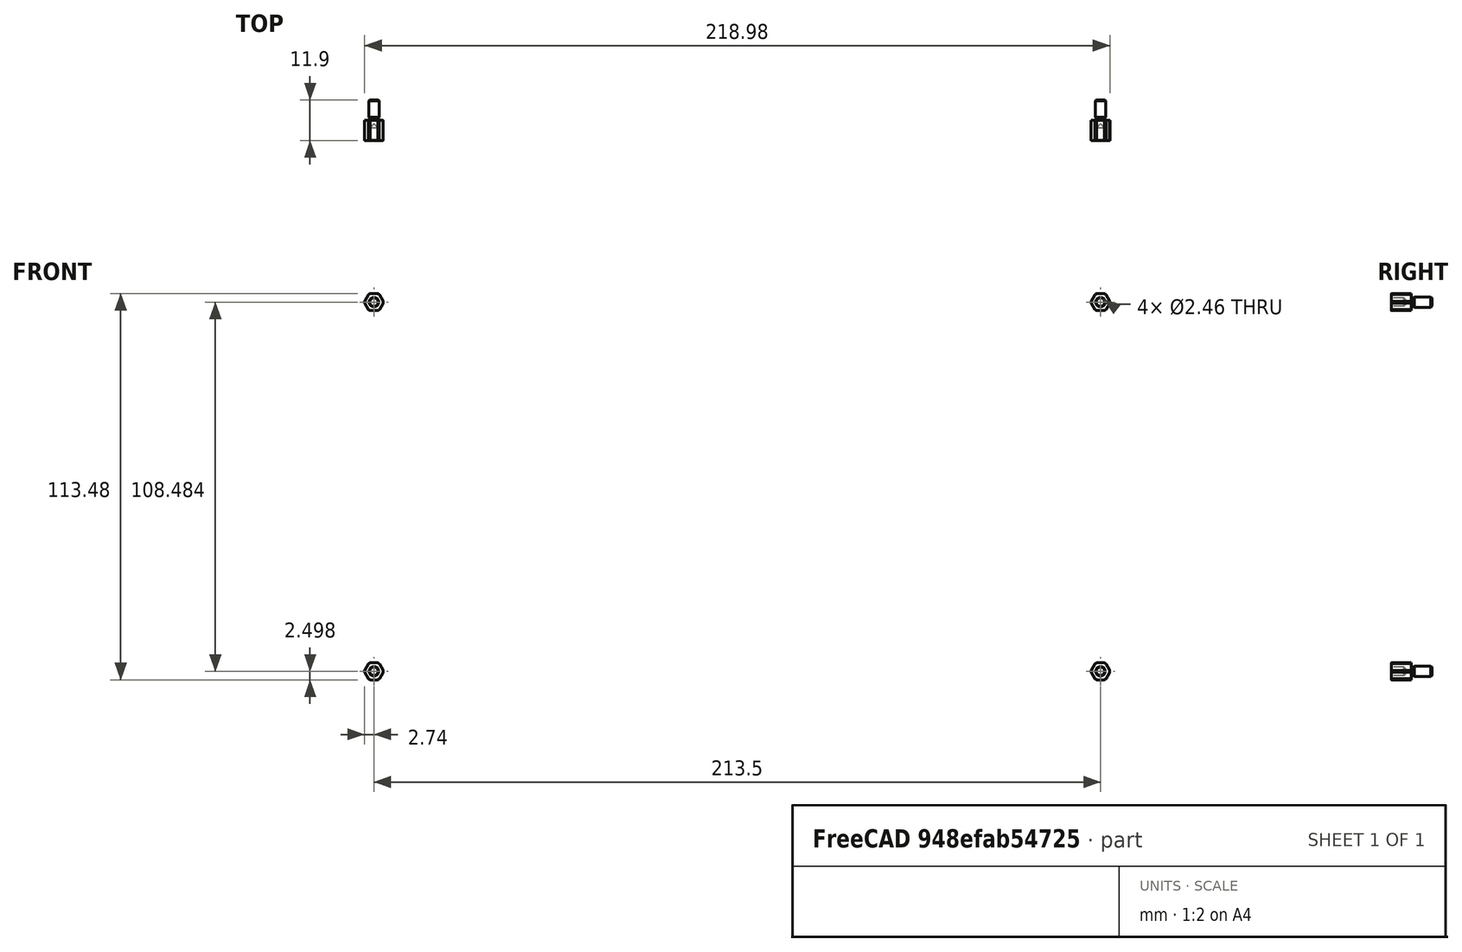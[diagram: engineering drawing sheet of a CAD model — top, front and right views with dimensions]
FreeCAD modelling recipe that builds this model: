
FCSTD DOCUMENT  (FreeCAD 1.0R38641 +468 (Git))
Label: enclosure
License: All rights reserved
LicenseURL: https://en.wikipedia.org/wiki/All_rights_reserved
objects: App::Link×58, App::FeaturePython×4, Assembly::AssemblyLink×4, Part::FeaturePython×4, Assembly::JointGroup×1, Assembly::AssemblyObject×1
note: 4 computed .brp shape members not serialized (recipe doc carries the construction recipe); baked Part::Feature solids carry a one-line shape summary decoded from their .brp
EXTERNAL_REF file=row.FCStd obj=Assembly
EXTERNAL_REF file=row.FCStd obj=ZRail84Hp
EXTERNAL_REF file=row.FCStd obj=ZRail84Hp001
EXTERNAL_REF file=row.FCStd obj=PanelSide
EXTERNAL_REF file=row.FCStd obj=PanelSide001
EXTERNAL_REF file=row.FCStd obj=PanelTopAndBottom
EXTERNAL_REF file=row.FCStd obj=PanelTopAndBottom001
EXTERNAL_REF file=row.FCStd obj=PanelBack
EXTERNAL_REF file=row.FCStd obj=FramePanelSpacer
EXTERNAL_REF file=row.FCStd obj=FramePanelSpacer001
EXTERNAL_REF file=row.FCStd obj=FrameBracket
EXTERNAL_REF file=row.FCStd obj=FrameBracket001
EXTERNAL_REF file=row.FCStd obj=FrameBracket002
EXTERNAL_REF file=row.FCStd obj=FrameBracket003
EXTERNAL_REF file=parts/dimensions.FCStd obj=VarSet
EXTERNAL_REF file=row.FCStd obj=BusBoard
EXTERNAL_REF file=psu.FCStd obj=Assembly
EXTERNAL_REF file=psu.FCStd obj=PsuTopAndBottom
EXTERNAL_REF file=psu.FCStd obj=PsuTopAndBottom001
EXTERNAL_REF file=psu.FCStd obj=PsuSideShort
EXTERNAL_REF file=psu.FCStd obj=PsuSideShort001
EXTERNAL_REF file=psu.FCStd obj=PsuSideLong
EXTERNAL_REF file=psu.FCStd obj=PsuSideLong001
EXTERNAL_REF file=psu.FCStd obj=PowerEntry
EXTERNAL_REF file=psu.FCStd obj=Psu
EXTERNAL_REF file=psu.FCStd obj=Standoff
EXTERNAL_REF file=psu.FCStd obj=Standoff001
EXTERNAL_REF file=psu.FCStd obj=Standoff002
EXTERNAL_REF file=psu.FCStd obj=Standoff003
EXTERNAL_REF file=psu.FCStd obj=Standoff004
EXTERNAL_REF file=psu.FCStd obj=Standoff005
EXTERNAL_REF file=psu.FCStd obj=Standoff006
EXTERNAL_REF file=psu.FCStd obj=Standoff007

FEATURE [App::Link] ZRail84Hp
  LinkedObject = -> <external row.FCStd>#ZRail84Hp
FEATURE [App::Link] ZRail84Hp001
  LinkPlacement = pos=(427,3.84e-14,-112.5) rot=(0,1,0;3.14159rad)
  LinkedObject = -> <external row.FCStd>#ZRail84Hp001
  Placement = pos=(427,3.84e-14,-112.5) rot=(0,1,0;3.14159rad)
FEATURE [App::Link] PanelSide
  LinkPlacement = pos=(2.1e-15,-4.56e-14,-3e-16) rot=(0,0,1;0rad)
  LinkedObject = -> <external row.FCStd>#PanelSide
  Placement = pos=(2.1e-15,-4.56e-14,-3e-16) rot=(0,0,1;0rad)
FEATURE [App::Link] PanelSide001
  LinkPlacement = pos=(428.854,-6e-16,4e-16) rot=(0,0,1;0rad)
  LinkedObject = -> <external row.FCStd>#PanelSide001
  Placement = pos=(428.854,-6e-16,4e-16) rot=(0,0,1;0rad)
FEATURE [App::Link] PanelTopAndBottom
  LinkPlacement = pos=(5.0165e-12,3e-16,-2.004e-13) rot=(0,0,1;0rad)
  LinkedObject = -> <external row.FCStd>#PanelTopAndBottom
  Placement = pos=(5.0165e-12,3e-16,-2.004e-13) rot=(0,0,1;0rad)
FEATURE [App::Link] PanelTopAndBottom001
  LinkPlacement = pos=(5.0396e-12,-3.3e-14,-122.5) rot=(0,0,1;0rad)
  LinkedObject = -> <external row.FCStd>#PanelTopAndBottom001
  Placement = pos=(5.0396e-12,-3.3e-14,-122.5) rot=(0,0,1;0rad)
FEATURE [App::Link] PanelBack
  LinkPlacement = pos=(5.0317e-12,1.81e-14,-2.019e-13) rot=(0,0,1;0rad)
  LinkedObject = -> <external row.FCStd>#PanelBack
  Placement = pos=(5.0317e-12,1.81e-14,-2.019e-13) rot=(0,0,1;0rad)
FEATURE [App::Link] FramePanelSpacer
  LinkPlacement = pos=(2.1e-15,-3.6e-14,-3.1e-15) rot=(0,0,1;0rad)
  LinkedObject = -> <external row.FCStd>#FramePanelSpacer
  Placement = pos=(2.1e-15,-3.6e-14,-3.1e-15) rot=(0,0,1;0rad)
FEATURE [App::Link] FramePanelSpacer001
  LinkPlacement = pos=(433.883,-1.9e-15,2.7e-15) rot=(0,0,1;0rad)
  LinkedObject = -> <external row.FCStd>#FramePanelSpacer001
  Placement = pos=(433.883,-1.9e-15,2.7e-15) rot=(0,0,1;0rad)
FEATURE [App::Link] FrameBracket
  LinkPlacement = pos=(-3.175,-3.44e-14,3.4e-15) rot=(0,0,1;0rad)
  LinkedObject = -> <external row.FCStd>#FrameBracket
  Placement = pos=(-3.175,-3.44e-14,3.4e-15) rot=(0,0,1;0rad)
FEATURE [App::Link] FrameBracket001
  LinkPlacement = pos=(-13.2334,-3.72e-14,-112.5) rot=(0,1,0;3.14159rad)
  LinkedObject = -> <external row.FCStd>#FrameBracket001
  Placement = pos=(-13.2334,-3.72e-14,-112.5) rot=(0,1,0;3.14159rad)
FEATURE [App::Link] FrameBracket002
  LinkPlacement = pos=(433.35,7.3e-15,-112.5) rot=(0,1,0;3.14159rad)
  LinkedObject = -> <external row.FCStd>#FrameBracket002
  Placement = pos=(433.35,7.3e-15,-112.5) rot=(0,1,0;3.14159rad)
FEATURE [App::Link] FrameBracket003
  LinkPlacement = pos=(437.058,3.9e-15,3.4e-15) rot=(0,0,1;0rad)
  LinkedObject = -> <external row.FCStd>#FrameBracket003
  Placement = pos=(437.058,3.9e-15,3.4e-15) rot=(0,0,1;0rad)
FEATURE [App::Link] ZRail84Hp002
  LinkedObject = -> <external row.FCStd>#ZRail84Hp
FEATURE [App::Link] ZRail84Hp003
  LinkPlacement = pos=(427,3.84e-14,-112.5) rot=(0,1,0;3.14159rad)
  LinkedObject = -> <external row.FCStd>#ZRail84Hp001
  Placement = pos=(427,3.84e-14,-112.5) rot=(0,1,0;3.14159rad)
FEATURE [App::Link] PanelSide002
  LinkPlacement = pos=(2.1e-15,-4.56e-14,-3e-16) rot=(0,0,1;0rad)
  LinkedObject = -> <external row.FCStd>#PanelSide
  Placement = pos=(2.1e-15,-4.56e-14,-3e-16) rot=(0,0,1;0rad)
FEATURE [App::Link] PanelSide003
  LinkPlacement = pos=(428.854,-6e-16,4e-16) rot=(0,0,1;0rad)
  LinkedObject = -> <external row.FCStd>#PanelSide001
  Placement = pos=(428.854,-6e-16,4e-16) rot=(0,0,1;0rad)
FEATURE [App::Link] PanelTopAndBottom002
  LinkPlacement = pos=(5.0165e-12,3e-16,-2.004e-13) rot=(0,0,1;0rad)
  LinkedObject = -> <external row.FCStd>#PanelTopAndBottom
  Placement = pos=(5.0165e-12,3e-16,-2.004e-13) rot=(0,0,1;0rad)
FEATURE [App::Link] PanelTopAndBottom003
  LinkPlacement = pos=(5.0396e-12,-3.3e-14,-122.5) rot=(0,0,1;0rad)
  LinkedObject = -> <external row.FCStd>#PanelTopAndBottom001
  Placement = pos=(5.0396e-12,-3.3e-14,-122.5) rot=(0,0,1;0rad)
FEATURE [App::Link] PanelBack001
  LinkPlacement = pos=(5.0317e-12,1.81e-14,-2.019e-13) rot=(0,0,1;0rad)
  LinkedObject = -> <external row.FCStd>#PanelBack
  Placement = pos=(5.0317e-12,1.81e-14,-2.019e-13) rot=(0,0,1;0rad)
FEATURE [App::Link] FramePanelSpacer002
  LinkPlacement = pos=(2.1e-15,-3.6e-14,-3.1e-15) rot=(0,0,1;0rad)
  LinkedObject = -> <external row.FCStd>#FramePanelSpacer
  Placement = pos=(2.1e-15,-3.6e-14,-3.1e-15) rot=(0,0,1;0rad)
FEATURE [App::Link] FramePanelSpacer003
  LinkPlacement = pos=(433.883,-1.9e-15,2.7e-15) rot=(0,0,1;0rad)
  LinkedObject = -> <external row.FCStd>#FramePanelSpacer001
  Placement = pos=(433.883,-1.9e-15,2.7e-15) rot=(0,0,1;0rad)
FEATURE [App::Link] FrameBracket004
  LinkPlacement = pos=(-3.175,-3.44e-14,3.4e-15) rot=(0,0,1;0rad)
  LinkedObject = -> <external row.FCStd>#FrameBracket
  Placement = pos=(-3.175,-3.44e-14,3.4e-15) rot=(0,0,1;0rad)
FEATURE [App::Link] FrameBracket005
  LinkPlacement = pos=(-13.2334,-3.72e-14,-112.5) rot=(0,1,0;3.14159rad)
  LinkedObject = -> <external row.FCStd>#FrameBracket001
  Placement = pos=(-13.2334,-3.72e-14,-112.5) rot=(0,1,0;3.14159rad)
FEATURE [App::Link] FrameBracket006
  LinkPlacement = pos=(433.35,7.3e-15,-112.5) rot=(0,1,0;3.14159rad)
  LinkedObject = -> <external row.FCStd>#FrameBracket002
  Placement = pos=(433.35,7.3e-15,-112.5) rot=(0,1,0;3.14159rad)
FEATURE [App::Link] FrameBracket007
  LinkPlacement = pos=(437.058,3.9e-15,3.4e-15) rot=(0,0,1;0rad)
  LinkedObject = -> <external row.FCStd>#FrameBracket003
  Placement = pos=(437.058,3.9e-15,3.4e-15) rot=(0,0,1;0rad)
FEATURE [App::FeaturePython] Joint  label="Fixed"  # Assembly joint (typed FeaturePython)
  Activated = true
  AngleMax = 0
  AngleMin = 0
  Detach1 = false
  Detach2 = false
  Distance = 0
  Distance2 = 0
  EnableAngleMax = false
  EnableAngleMin = false
  EnableLengthMax = false
  EnableLengthMin = false
  JointType = 0 (Fixed)
  LengthMax = 0
  LengthMin = 0
  Placement1 = pos=(-1.8542,-10.527,11.2) rot=(0.57735,0.57735,0.57735;2.0944rad)
  Placement2 = pos=(-1.8542,-10.527,11.2) rot=(0.57735,0.57735,0.57735;2.0944rad)
  Reference1 = -> Assembly [Row.FrameBracket003.Edge92,Row.FrameBracket003.Edge92]
  Reference2 = -> Assembly [Row001.FrameBracket006.Edge92,Row001.FrameBracket006.Edge92]
FEATURE [App::Link] ZRail84Hp004
  LinkedObject = -> <external row.FCStd>#ZRail84Hp
FEATURE [App::Link] ZRail84Hp005
  LinkPlacement = pos=(427,3.84e-14,-112.5) rot=(0,1,0;3.14159rad)
  LinkedObject = -> <external row.FCStd>#ZRail84Hp001
  Placement = pos=(427,3.84e-14,-112.5) rot=(0,1,0;3.14159rad)
FEATURE [App::Link] PanelSide004
  LinkPlacement = pos=(2.1e-15,-4.56e-14,-3e-16) rot=(0,0,1;0rad)
  LinkedObject = -> <external row.FCStd>#PanelSide
  Placement = pos=(2.1e-15,-4.56e-14,-3e-16) rot=(0,0,1;0rad)
FEATURE [App::Link] PanelSide005
  LinkPlacement = pos=(428.854,-6e-16,4e-16) rot=(0,0,1;0rad)
  LinkedObject = -> <external row.FCStd>#PanelSide001
  Placement = pos=(428.854,-6e-16,4e-16) rot=(0,0,1;0rad)
FEATURE [App::Link] PanelTopAndBottom004
  LinkPlacement = pos=(5.0165e-12,3e-16,-2.004e-13) rot=(0,0,1;0rad)
  LinkedObject = -> <external row.FCStd>#PanelTopAndBottom
  Placement = pos=(5.0165e-12,3e-16,-2.004e-13) rot=(0,0,1;0rad)
FEATURE [App::Link] PanelTopAndBottom005
  LinkPlacement = pos=(5.0396e-12,-3.3e-14,-122.5) rot=(0,0,1;0rad)
  LinkedObject = -> <external row.FCStd>#PanelTopAndBottom001
  Placement = pos=(5.0396e-12,-3.3e-14,-122.5) rot=(0,0,1;0rad)
FEATURE [App::Link] PanelBack002
  LinkPlacement = pos=(5.0317e-12,1.81e-14,-2.019e-13) rot=(0,0,1;0rad)
  LinkedObject = -> <external row.FCStd>#PanelBack
  Placement = pos=(5.0317e-12,1.81e-14,-2.019e-13) rot=(0,0,1;0rad)
FEATURE [App::Link] FramePanelSpacer004
  LinkPlacement = pos=(2.1e-15,-3.6e-14,-3.1e-15) rot=(0,0,1;0rad)
  LinkedObject = -> <external row.FCStd>#FramePanelSpacer
  Placement = pos=(2.1e-15,-3.6e-14,-3.1e-15) rot=(0,0,1;0rad)
FEATURE [App::Link] FramePanelSpacer005
  LinkPlacement = pos=(433.883,-1.9e-15,2.7e-15) rot=(0,0,1;0rad)
  LinkedObject = -> <external row.FCStd>#FramePanelSpacer001
  Placement = pos=(433.883,-1.9e-15,2.7e-15) rot=(0,0,1;0rad)
FEATURE [App::Link] FrameBracket008
  LinkPlacement = pos=(-3.175,-3.44e-14,3.4e-15) rot=(0,0,1;0rad)
  LinkedObject = -> <external row.FCStd>#FrameBracket
  Placement = pos=(-3.175,-3.44e-14,3.4e-15) rot=(0,0,1;0rad)
FEATURE [App::Link] FrameBracket009
  LinkPlacement = pos=(-13.2334,-3.72e-14,-112.5) rot=(0,1,0;3.14159rad)
  LinkedObject = -> <external row.FCStd>#FrameBracket001
  Placement = pos=(-13.2334,-3.72e-14,-112.5) rot=(0,1,0;3.14159rad)
FEATURE [App::Link] FrameBracket010
  LinkPlacement = pos=(433.35,7.3e-15,-112.5) rot=(0,1,0;3.14159rad)
  LinkedObject = -> <external row.FCStd>#FrameBracket002
  Placement = pos=(433.35,7.3e-15,-112.5) rot=(0,1,0;3.14159rad)
FEATURE [App::Link] FrameBracket011
  LinkPlacement = pos=(437.058,3.9e-15,3.4e-15) rot=(0,0,1;0rad)
  LinkedObject = -> <external row.FCStd>#FrameBracket003
  Placement = pos=(437.058,3.9e-15,3.4e-15) rot=(0,0,1;0rad)
FEATURE [App::FeaturePython] Joint001  label="Fixed001"  # Assembly joint (typed FeaturePython)
  Activated = true
  AngleMax = 0
  AngleMin = 0
  Detach1 = false
  Detach2 = false
  Distance = 0
  Distance2 = 0
  EnableAngleMax = false
  EnableAngleMin = false
  EnableLengthMax = false
  EnableLengthMin = false
  JointType = 0 (Fixed)
  LengthMax = 0
  LengthMin = 0
  Offset2 = pos=(0,0,0) rot=(0,0,1;0.392699rad)
  Placement1 = pos=(-1.8542,-10.3247,9.14628) rot=(0.57735,0.57735,0.57735;2.0944rad)
  Placement2 = pos=(-1.8542,-10.3247,9.14628) rot=(0.639338,0.427192,0.639338;2.33414rad)
  Reference1 = -> Assembly [Row002.FrameBracket010.Edge87,Row002.FrameBracket010.Edge87]
  Reference2 = -> Assembly [Row001.FrameBracket007.Edge87,Row001.FrameBracket007.Edge87]
  expr: .Offset2.Rotation.Yaw = dimensions#VarSet.MaxAngle
FEATURE [App::Link] BusBoard
  LinkPlacement = pos=(17.92,121.373,-77.205) rot=(1,0,0;1.5708rad)
  LinkedObject = -> <external row.FCStd>#BusBoard
  Placement = pos=(17.92,121.373,-77.205) rot=(1,0,0;1.5708rad)
FEATURE [Assembly::AssemblyLink] Row
  Group = -> [ZRail84Hp,ZRail84Hp001,PanelSide,PanelSide001,PanelTopAndBottom,PanelTopAndBottom001,PanelBack,FramePanelSpacer,FramePanelSpacer001,FrameBracket,FrameBracket001,FrameBracket002,FrameBracket003,BusBoard]
  LinkedObject = -> <external row.FCStd>#Assembly
  Origin = -> Origin001
  Rigid = true
FEATURE [App::FeaturePython] GroundedJoint  # Assembly grounded joint (typed FeaturePython)
  ObjectToGround = -> Row
FEATURE [App::Link] BusBoard001
  LinkPlacement = pos=(17.92,121.373,-77.205) rot=(1,0,0;1.5708rad)
  LinkedObject = -> <external row.FCStd>#BusBoard
  Placement = pos=(17.92,121.373,-77.205) rot=(1,0,0;1.5708rad)
FEATURE [Assembly::AssemblyLink] Row001
  Group = -> [ZRail84Hp002,ZRail84Hp003,PanelSide002,PanelSide003,PanelTopAndBottom002,PanelTopAndBottom003,PanelBack001,FramePanelSpacer002,FramePanelSpacer003,FrameBracket004,FrameBracket005,FrameBracket006,FrameBracket007,BusBoard001]
  LinkedObject = -> <external row.FCStd>#Assembly
  Origin = -> Origin002
  Placement = pos=(2.03e-14,4.768e-13,134.9) rot=(0,0,1;0rad)
  Rigid = true
FEATURE [App::Link] BusBoard002
  LinkPlacement = pos=(17.92,121.373,-77.205) rot=(1,0,0;1.5708rad)
  LinkedObject = -> <external row.FCStd>#BusBoard
  Placement = pos=(17.92,121.373,-77.205) rot=(1,0,0;1.5708rad)
FEATURE [Assembly::AssemblyLink] Row002
  Group = -> [ZRail84Hp004,ZRail84Hp005,PanelSide004,PanelSide005,PanelTopAndBottom004,PanelTopAndBottom005,PanelBack002,FramePanelSpacer004,FramePanelSpacer005,FrameBracket008,FrameBracket009,FrameBracket010,FrameBracket011,BusBoard002]
  LinkedObject = -> <external row.FCStd>#Assembly
  Origin = -> Origin003
  Placement = pos=(-2.818e-13,-47.3379,260.384) rot=(1,0,0;0.392699rad)
  Rigid = true
FEATURE [Part::FeaturePython] Standoff  label="M3x6x5-Standoff"  # WARN: FeaturePython — macro-defined, semantics opaque (R4)
  BaseObject = -> Row001 [PanelBack001.Pad.Edge218]
  Diameter = 2
  Invert = false
  LeftHanded = false
  Length = 4
  LengthCustom = 6
  MatchOuter = false
  Offset = -6
  OffsetAngle = 0
  Placement = pos=(320.25,133.227,132.892) rot=(1,0,0;1.5708rad)
  ScrewLength = 6
  Thread = false
  Type = 0
  Width = 0
FEATURE [Part::FeaturePython] Standoff001  label="M3x6x5-Standoff028"  # WARN: FeaturePython — macro-defined, semantics opaque (R4)
  BaseObject = -> Row001 [PanelBack001.Pad.Edge245]
  Diameter = 2
  Invert = false
  LeftHanded = false
  Length = 4
  LengthCustom = 6
  MatchOuter = false
  Offset = -6
  OffsetAngle = 0
  Placement = pos=(106.75,133.227,132.892) rot=(1,0,0;1.5708rad)
  ScrewLength = 6
  Thread = false
  Type = 0
  Width = 0
FEATURE [Part::FeaturePython] Standoff002  label="M3x6x5-Standoff029"  # WARN: FeaturePython — macro-defined, semantics opaque (R4)
  BaseObject = -> Row001 [PanelBack001.Pad.Edge221]
  Diameter = 2
  Invert = false
  LeftHanded = false
  Length = 4
  LengthCustom = 6
  MatchOuter = false
  Offset = -6
  OffsetAngle = 0
  Placement = pos=(320.25,133.227,24.4081) rot=(1,0,0;1.5708rad)
  ScrewLength = 6
  Thread = false
  Type = 0
  Width = 0
FEATURE [Part::FeaturePython] Standoff003  label="M3x6x5-Standoff030"  # WARN: FeaturePython — macro-defined, semantics opaque (R4)
  BaseObject = -> Row001 [PanelBack001.Pad.Edge248]
  Diameter = 2
  Invert = false
  LeftHanded = false
  Length = 4
  LengthCustom = 6
  MatchOuter = false
  Offset = -6
  OffsetAngle = 0
  Placement = pos=(106.75,133.227,24.4081) rot=(1,0,0;1.5708rad)
  ScrewLength = 6
  Thread = false
  Type = 0
  Width = 0
FEATURE [App::Link] PsuTopAndBottom
  LinkedObject = -> <external psu.FCStd>#PsuTopAndBottom
FEATURE [App::Link] PsuTopAndBottom001
  LinkPlacement = pos=(-6e-15,-51.8542,-3e-16) rot=(0,0,1;0rad)
  LinkedObject = -> <external psu.FCStd>#PsuTopAndBottom001
  Placement = pos=(-6e-15,-51.8542,-3e-16) rot=(0,0,1;0rad)
FEATURE [App::Link] PsuSideShort
  LinkPlacement = pos=(0.127,-51.8542,1.5e-14) rot=(0,0,1;0rad)
  LinkedObject = -> <external psu.FCStd>#PsuSideShort
  Placement = pos=(0.127,-51.8542,1.5e-14) rot=(0,0,1;0rad)
FEATURE [App::Link] PsuSideShort001
  LinkPlacement = pos=(-227.198,-51.8542,1.832e-13) rot=(0,0,1;0rad)
  LinkedObject = -> <external psu.FCStd>#PsuSideShort001
  Placement = pos=(-227.198,-51.8542,1.832e-13) rot=(0,0,1;0rad)
FEATURE [App::Link] PsuSideLong
  LinkPlacement = pos=(2.22e-14,-51.8542,0.127) rot=(0,0,1;0rad)
  LinkedObject = -> <external psu.FCStd>#PsuSideLong
  Placement = pos=(2.22e-14,-51.8542,0.127) rot=(0,0,1;0rad)
FEATURE [App::Link] PsuSideLong001
  LinkPlacement = pos=(2.26e-14,-51.8542,-86.1976) rot=(0,0,1;0rad)
  LinkedObject = -> <external psu.FCStd>#PsuSideLong001
  Placement = pos=(2.26e-14,-51.8542,-86.1976) rot=(0,0,1;0rad)
FEATURE [App::Link] PowerEntry
  LinkPlacement = pos=(333.089,127.227,-56.25) rot=(0,0.707107,-0.707107;3.14159rad)
  LinkedObject = -> <external psu.FCStd>#PowerEntry
  Placement = pos=(333.089,127.227,-56.25) rot=(0,0.707107,-0.707107;3.14159rad)
FEATURE [App::Link] Psu
  LinkPlacement = pos=(103,83.2271,-16.25) rot=(-1,0,0;1.5708rad)
  LinkedObject = -> <external psu.FCStd>#Psu
  Placement = pos=(103,83.2271,-16.25) rot=(-1,0,0;1.5708rad)
FEATURE [App::Link] Standoff004  label="M3x6x5-Standoff013"
  LinkPlacement = pos=(274.5,83.2271,-21.35) rot=(1,0,0;1.5708rad)
  LinkedObject = -> <external psu.FCStd>#Standoff
  Placement = pos=(274.5,83.2271,-21.35) rot=(1,0,0;1.5708rad)
FEATURE [App::Link] Standoff005  label="M3x6x5-Standoff016"
  LinkPlacement = pos=(122.1,83.2271,-36.55) rot=(1,0,0;1.5708rad)
  LinkedObject = -> <external psu.FCStd>#Standoff001
  Placement = pos=(122.1,83.2271,-36.55) rot=(1,0,0;1.5708rad)
FEATURE [App::Link] Standoff006  label="M3x6x5-Standoff017"
  LinkPlacement = pos=(122.1,83.2271,-75.95) rot=(1,0,0;1.5708rad)
  LinkedObject = -> <external psu.FCStd>#Standoff002
  Placement = pos=(122.1,83.2271,-75.95) rot=(1,0,0;1.5708rad)
FEATURE [App::Link] Standoff007  label="M3x6x5-Standoff018"
  LinkPlacement = pos=(274.5,83.2271,-91.15) rot=(1,0,0;1.5708rad)
  LinkedObject = -> <external psu.FCStd>#Standoff003
  Placement = pos=(274.5,83.2271,-91.15) rot=(1,0,0;1.5708rad)
FEATURE [App::Link] Standoff008  label="M3x50x5-Standoff"
  LinkPlacement = pos=(320.25,127.227,-2.0081) rot=(1,0,0;1.5708rad)
  LinkedObject = -> <external psu.FCStd>#Standoff004
  Placement = pos=(320.25,127.227,-2.0081) rot=(1,0,0;1.5708rad)
FEATURE [App::Link] Standoff009  label="M3x50x5-Standoff004"
  LinkPlacement = pos=(106.75,127.227,-2.0081) rot=(1,0,0;1.5708rad)
  LinkedObject = -> <external psu.FCStd>#Standoff005
  Placement = pos=(106.75,127.227,-2.0081) rot=(1,0,0;1.5708rad)
FEATURE [App::Link] Standoff010  label="M3x50x5-Standoff005"
  LinkPlacement = pos=(320.25,127.227,-110.492) rot=(1,0,0;1.5708rad)
  LinkedObject = -> <external psu.FCStd>#Standoff006
  Placement = pos=(320.25,127.227,-110.492) rot=(1,0,0;1.5708rad)
FEATURE [App::Link] Standoff011  label="M3x50x5-Standoff006"
  LinkPlacement = pos=(106.75,127.227,-110.492) rot=(1,0,0;1.5708rad)
  LinkedObject = -> <external psu.FCStd>#Standoff007
  Placement = pos=(106.75,127.227,-110.492) rot=(1,0,0;1.5708rad)
FEATURE [Assembly::AssemblyLink] PsuAssembly
  Group = -> [PsuTopAndBottom,PsuTopAndBottom001,PsuSideShort,PsuSideShort001,PsuSideLong,PsuSideLong001,PowerEntry,Psu,Standoff004,Standoff005,Standoff006,Standoff007,Standoff008,Standoff009,Standoff010,Standoff011]
  LinkedObject = -> <external psu.FCStd>#Assembly
  Origin = -> Origin004
  Placement = pos=(5.1291e-12,57.8542,134.9) rot=(0,0,1;0rad)
  Rigid = true
FEATURE [App::FeaturePython] Joint005  label="Fixed005"  # Assembly joint (typed FeaturePython)
  Activated = true
  AngleMax = 0
  AngleMin = 0
  Detach1 = false
  Detach2 = false
  Distance = 0
  Distance2 = 0
  EnableAngleMax = false
  EnableAngleMin = false
  EnableLengthMax = false
  EnableLengthMin = false
  JointType = 0 (Fixed)
  LengthMax = 0
  LengthMin = 0
  Offset2 = pos=(0,0,-6) rot=(0,0,1;3.14159rad)
  Placement1 = pos=(106.75,127.227,-110.492) rot=(0,0.707107,0.707107;3.14159rad)
  Placement2 = pos=(106.75,133.227,-110.492) rot=(0,-0.707107,0.707107;3.14159rad)
  Reference1 = -> Assembly [PsuAssembly.PsuTopAndBottom001.Edge176,PsuAssembly.PsuTopAndBottom001.Edge176]
  Reference2 = -> Assembly [Row001.PanelBack001.Edge248,Row001.PanelBack001.Edge248]
FEATURE [Assembly::JointGroup] Joints
  Group = -> [GroundedJoint,Joint,Joint001,Joint005]
FEATURE [Assembly::AssemblyObject] Assembly  label="Enclosure"
  Group = -> [Joints,Row,GroundedJoint,Row001,Joint,Row002,Joint001,Standoff,Standoff001,Standoff002,Standoff003,PsuAssembly,Joint005]
  Origin = -> Origin
  Type = Assembly

RESOLVED EXTERNAL PARTS (link-assembly join: the EXTERNAL_REF files above that resolve inside this repo's crawl, each included once):
---- part psu.FCStd = doc fcstd_034335b4882d ----
FCSTD DOCUMENT  (FreeCAD 1.0R38641 +468 (Git))
Label: psu
License: All rights reserved
LicenseURL: https://en.wikipedia.org/wiki/All_rights_reserved
objects: App::Link×8, App::FeaturePython×8, Part::FeaturePython×8, Assembly::JointGroup×1, Assembly::AssemblyObject×1
note: 8 computed .brp shape members not serialized (recipe doc carries the construction recipe); baked Part::Feature solids carry a one-line shape summary decoded from their .brp
EXTERNAL_REF file=parts/psu/psu_top_and_bottom.FCStd obj=Body
EXTERNAL_REF file=parts/psu/psu_side_short.FCStd obj=Body
EXTERNAL_REF file=parts/psu/psu_side_long.FCStd obj=Body
EXTERNAL_REF file=third_party/qualtek_power_entry.FCStd obj=Body
EXTERNAL_REF file=parts/dimensions.FCStd obj=VarSet
EXTERNAL_REF file=third_party/doepfer_psu3.FCStd obj=Body

FEATURE [App::Link] PsuTopAndBottom
  LinkedObject = -> <external parts/psu/psu_top_and_bottom.FCStd>#Body
FEATURE [App::FeaturePython] GroundedJoint  # Assembly grounded joint (typed FeaturePython)
  ObjectToGround = -> PsuTopAndBottom
FEATURE [App::Link] PsuTopAndBottom001
  LinkPlacement = pos=(-6e-15,-51.8542,-3e-16) rot=(0,0,1;0rad)
  LinkedObject = -> <external parts/psu/psu_top_and_bottom.FCStd>#Body
  Placement = pos=(-6e-15,-51.8542,-3e-16) rot=(0,0,1;0rad)
FEATURE [App::Link] PsuSideShort
  LinkPlacement = pos=(0.127,-51.8542,1.5e-14) rot=(0,0,1;0rad)
  LinkedObject = -> <external parts/psu/psu_side_short.FCStd>#Body
  Placement = pos=(0.127,-51.8542,1.5e-14) rot=(0,0,1;0rad)
FEATURE [App::Link] PsuSideShort001
  LinkPlacement = pos=(-227.198,-51.8542,1.832e-13) rot=(0,0,1;0rad)
  LinkedObject = -> <external parts/psu/psu_side_short.FCStd>#Body
  Placement = pos=(-227.198,-51.8542,1.832e-13) rot=(0,0,1;0rad)
FEATURE [App::Link] PsuSideLong
  LinkPlacement = pos=(2.22e-14,-51.8542,0.127) rot=(0,0,1;0rad)
  LinkedObject = -> <external parts/psu/psu_side_long.FCStd>#Body
  Placement = pos=(2.22e-14,-51.8542,0.127) rot=(0,0,1;0rad)
FEATURE [App::Link] PsuSideLong001
  LinkPlacement = pos=(2.26e-14,-51.8542,-86.1976) rot=(0,0,1;0rad)
  LinkedObject = -> <external parts/psu/psu_side_long.FCStd>#Body
  Placement = pos=(2.26e-14,-51.8542,-86.1976) rot=(0,0,1;0rad)
FEATURE [App::Link] PowerEntry
  LinkPlacement = pos=(333.089,127.227,-56.25) rot=(0,0.707107,-0.707107;3.14159rad)
  LinkedObject = -> <external third_party/qualtek_power_entry.FCStd>#Body
  Placement = pos=(333.089,127.227,-56.25) rot=(0,0.707107,-0.707107;3.14159rad)
FEATURE [App::FeaturePython] Joint  label="Fixed"  # Assembly joint (typed FeaturePython)
  Activated = true
  AngleMax = 0
  AngleMin = 0
  Detach1 = false
  Detach2 = false
  Distance = 0
  Distance2 = 0
  EnableAngleMax = false
  EnableAngleMin = false
  EnableLengthMax = false
  EnableLengthMin = false
  JointType = 0 (Fixed)
  LengthMax = 0
  LengthMin = 0
  Offset2 = pos=(0.127,0,0.127) rot=(0,0,1;0rad)
  Placement1 = pos=(328.216,127.227,-24.579) rot=(0,0,1;0rad)
  Placement2 = pos=(328.089,179.081,-24.579) rot=(0,0,1;0rad)
  Reference1 = -> Assembly [PsuTopAndBottom.Vertex91,PsuTopAndBottom.Vertex91]
  Reference2 = -> Assembly [PsuSideShort.Vertex42,PsuSideShort.Vertex42]
  expr: .Offset2.Base.x = dimensions#VarSet.EnclosureFinishThickness
  expr: .Offset2.Base.z = dimensions#VarSet.EnclosureFinishThickness
FEATURE [App::FeaturePython] Joint001  label="Fixed001"  # Assembly joint (typed FeaturePython)
  Activated = true
  AngleMax = 0
  AngleMin = 0
  Detach1 = false
  Detach2 = false
  Distance = 0
  Distance2 = 0
  EnableAngleMax = false
  EnableAngleMin = false
  EnableLengthMax = false
  EnableLengthMin = false
  JointType = 0 (Fixed)
  LengthMax = 0
  LengthMin = 0
  Offset1 = pos=(0.127,0,0.127) rot=(0,0,1;0rad)
  Placement1 = pos=(328.089,179.081,-24.579) rot=(0,0,1;0rad)
  Placement2 = pos=(100.892,127.227,-24.579) rot=(0,0,1;0rad)
  Reference1 = -> Assembly [PsuSideShort001.Vertex42,PsuSideShort001.Vertex42]
  Reference2 = -> Assembly [PsuTopAndBottom.Vertex67,PsuTopAndBottom.Vertex67]
  expr: .Offset1.Base.x = dimensions#VarSet.EnclosureFinishThickness
  expr: .Offset1.Base.z = dimensions#VarSet.EnclosureFinishThickness
FEATURE [App::FeaturePython] Joint002  label="Fixed002"  # Assembly joint (typed FeaturePython)
  Activated = true
  AngleMax = 0
  AngleMin = 0
  Detach1 = false
  Detach2 = false
  Distance = 0
  Distance2 = 0
  EnableAngleMax = false
  EnableAngleMin = false
  EnableLengthMax = false
  EnableLengthMin = false
  JointType = 0 (Fixed)
  LengthMax = 0
  LengthMin = 0
  Offset2 = pos=(0.127,0,0.127) rot=(0,0,1;0rad)
  Placement1 = pos=(328.216,127.227,-24.579) rot=(0,0,1;0rad)
  Placement2 = pos=(328.089,127.227,-24.579) rot=(0,0,1;0rad)
  Reference1 = -> Assembly [PsuTopAndBottom001.Vertex91,PsuTopAndBottom001.Vertex91]
  Reference2 = -> Assembly [PsuSideShort.Vertex10,PsuSideShort.Vertex10]
  expr: .Offset2.Base.x = dimensions#VarSet.EnclosureFinishThickness
  expr: .Offset2.Base.z = dimensions#VarSet.EnclosureFinishThickness
FEATURE [App::FeaturePython] Joint003  label="Fixed003"  # Assembly joint (typed FeaturePython)
  Activated = true
  AngleMax = 0
  AngleMin = 0
  Detach1 = false
  Detach2 = false
  Distance = 0
  Distance2 = 0
  EnableAngleMax = false
  EnableAngleMin = false
  EnableLengthMax = false
  EnableLengthMin = false
  JointType = 0 (Fixed)
  LengthMax = 0
  LengthMin = 0
  Offset1 = pos=(0.127,0,0.127) rot=(0,0,1;0rad)
  Placement1 = pos=(303.647,127.227,-12.1606) rot=(0,0,1;0rad)
  Placement2 = pos=(303.647,127.227,-12.0336) rot=(0,0,1;0rad)
  Reference1 = -> Assembly [PsuSideLong.Vertex28,PsuSideLong.Vertex28]
  Reference2 = -> Assembly [PsuTopAndBottom001.Vertex105,PsuTopAndBottom001.Vertex105]
  expr: .Offset1.Base.x = dimensions#VarSet.EnclosureFinishThickness
  expr: .Offset1.Base.z = dimensions#VarSet.EnclosureFinishThickness
FEATURE [App::FeaturePython] Joint004  label="Fixed004"  # Assembly joint (typed FeaturePython)
  Activated = true
  AngleMax = 0
  AngleMin = 0
  Detach1 = false
  Detach2 = false
  Distance = 0
  Distance2 = 0
  EnableAngleMax = false
  EnableAngleMin = false
  EnableLengthMax = false
  EnableLengthMin = false
  JointType = 0 (Fixed)
  LengthMax = 0
  LengthMin = 0
  Offset1 = pos=(-0.127,0,-0.127) rot=(0,0,1;0rad)
  Placement1 = pos=(303.52,127.227,-98.4852) rot=(0,0,1;0rad)
  Placement2 = pos=(303.52,127.227,-12.2876) rot=(0,0,1;0rad)
  Reference1 = -> Assembly [PsuTopAndBottom001.Vertex97,PsuTopAndBottom001.Vertex97]
  Reference2 = -> Assembly [PsuSideLong001.Vertex28,PsuSideLong001.Vertex28]
  expr: .Offset1.Base.x = -dimensions#VarSet.EnclosureFinishThickness
  expr: .Offset1.Base.z = -dimensions#VarSet.EnclosureFinishThickness
FEATURE [App::FeaturePython] Joint007  label="Fixed007"  # Assembly joint (typed FeaturePython)
  Activated = true
  AngleMax = 0
  AngleMin = 0
  Detach1 = false
  Detach2 = false
  Distance = 0
  Distance2 = 0
  EnableAngleMax = false
  EnableAngleMin = false
  EnableLengthMax = false
  EnableLengthMin = false
  JointType = 0 (Fixed)
  LengthMax = 0
  LengthMin = 0
  Offset2 = pos=(0,0,0) rot=(0,0,-1;1.5708rad)
  Placement1 = pos=(5,-7.1e-15,5) rot=(-0.57735,-0.57735,0.57735;2.0944rad)
  Placement2 = pos=(327.962,174.081,-56.25) rot=(0,1,0;1.5708rad)
  Reference1 = -> Assembly [PowerEntry.Edge36,PowerEntry.Edge36]
  Reference2 = -> Assembly [PsuSideShort.Edge123,PsuSideShort.Edge123]
FEATURE [Part::FeaturePython] Standoff  label="M3x6x5-Standoff"  # WARN: FeaturePython — macro-defined, semantics opaque (R4)
  BaseObject = -> PsuTopAndBottom001 [Pad.Edge183]
  Diameter = 2
  Invert = true
  LeftHanded = false
  Length = 4
  LengthCustom = 6
  MatchOuter = false
  Offset = -6
  OffsetAngle = 0
  Placement = pos=(274.5,83.2271,-21.35) rot=(1,0,0;1.5708rad)
  ScrewLength = 6
  Thread = false
  Type = 0
  Width = 0
FEATURE [Part::FeaturePython] Standoff001  label="M3x6x5-Standoff019"  # WARN: FeaturePython — macro-defined, semantics opaque (R4)
  BaseObject = -> PsuTopAndBottom001 [Pad.Edge186]
  Diameter = 2
  Invert = true
  LeftHanded = false
  Length = 4
  LengthCustom = 6
  MatchOuter = false
  Offset = -6
  OffsetAngle = 0
  Placement = pos=(122.1,83.2271,-36.55) rot=(1,0,0;1.5708rad)
  ScrewLength = 6
  Thread = false
  Type = 0
  Width = 0
FEATURE [Part::FeaturePython] Standoff002  label="M3x6x5-Standoff020"  # WARN: FeaturePython — macro-defined, semantics opaque (R4)
  BaseObject = -> PsuTopAndBottom001 [Pad.Edge192]
  Diameter = 2
  Invert = true
  LeftHanded = false
  Length = 4
  LengthCustom = 6
  MatchOuter = false
  Offset = -6
  OffsetAngle = 0
  Placement = pos=(122.1,83.2271,-75.95) rot=(1,0,0;1.5708rad)
  ScrewLength = 6
  Thread = false
  Type = 0
  Width = 0
FEATURE [Part::FeaturePython] Standoff003  label="M3x6x5-Standoff021"  # WARN: FeaturePython — macro-defined, semantics opaque (R4)
  BaseObject = -> PsuTopAndBottom001 [Pad.Edge189]
  Diameter = 2
  Invert = true
  LeftHanded = false
  Length = 4
  LengthCustom = 6
  MatchOuter = false
  Offset = -6
  OffsetAngle = 0
  Placement = pos=(274.5,83.2271,-91.15) rot=(1,0,0;1.5708rad)
  ScrewLength = 6
  Thread = false
  Type = 0
  Width = 0
FEATURE [App::Link] Psu
  LinkPlacement = pos=(103,83.2271,-16.25) rot=(-1,0,0;1.5708rad)
  LinkedObject = -> <external third_party/doepfer_psu3.FCStd>#Body
  Placement = pos=(103,83.2271,-16.25) rot=(-1,0,0;1.5708rad)
FEATURE [App::FeaturePython] Joint008  label="Fixed008"  # Assembly joint (typed FeaturePython)
  Activated = true
  AngleMax = 0
  AngleMin = 0
  Detach1 = false
  Detach2 = false
  Distance = 0
  Distance2 = 0
  EnableAngleMax = false
  EnableAngleMin = false
  EnableLengthMax = false
  EnableLengthMin = false
  JointType = 0 (Fixed)
  LengthMax = 0
  LengthMin = 0
  Offset1 = pos=(0,0,-6) rot=(0,-1,0;3.14159rad)
  Placement1 = pos=(19.1,20.3,-6) rot=(0,-1,0;3.14159rad)
  Placement2 = pos=(122.1,129.081,-36.55) rot=(0,0.707107,0.707107;3.14159rad)
  Reference1 = -> Assembly [Psu.Edge20,Psu.Edge20]
  Reference2 = -> Assembly [PsuTopAndBottom001.Edge186,PsuTopAndBottom001.Edge186]
FEATURE [Assembly::JointGroup] Joints
  Group = -> [GroundedJoint,Joint,Joint001,Joint002,Joint003,Joint004,Joint007,Joint008]
FEATURE [Part::FeaturePython] Standoff004  label="M3x50x5-Standoff"  # WARN: FeaturePython — macro-defined, semantics opaque (R4)
  BaseObject = -> PsuTopAndBottom001 [Pad.Edge174]
  Diameter = 2
  Invert = true
  LeftHanded = false
  Length = 4
  LengthCustom = 50
  MatchOuter = false
  Offset = -50
  OffsetAngle = 0
  Placement = pos=(320.25,127.227,-2.0081) rot=(1,0,0;1.5708rad)
  ScrewLength = 6
  Thread = false
  Type = 0
  Width = 0
FEATURE [Part::FeaturePython] Standoff005  label="M3x50x5-Standoff007"  # WARN: FeaturePython — macro-defined, semantics opaque (R4)
  BaseObject = -> PsuTopAndBottom001 [Pad.Edge180]
  Diameter = 2
  Invert = true
  LeftHanded = false
  Length = 4
  LengthCustom = 50
  MatchOuter = false
  Offset = -50
  OffsetAngle = 0
  Placement = pos=(106.75,127.227,-2.0081) rot=(1,0,0;1.5708rad)
  ScrewLength = 6
  Thread = false
  Type = 0
  Width = 0
FEATURE [Part::FeaturePython] Standoff006  label="M3x50x5-Standoff008"  # WARN: FeaturePython — macro-defined, semantics opaque (R4)
  BaseObject = -> PsuTopAndBottom001 [Pad.Edge171]
  Diameter = 2
  Invert = true
  LeftHanded = false
  Length = 4
  LengthCustom = 50
  MatchOuter = false
  Offset = -50
  OffsetAngle = 0
  Placement = pos=(320.25,127.227,-110.492) rot=(1,0,0;1.5708rad)
  ScrewLength = 6
  Thread = false
  Type = 0
  Width = 0
FEATURE [Part::FeaturePython] Standoff007  label="M3x50x5-Standoff009"  # WARN: FeaturePython — macro-defined, semantics opaque (R4)
  BaseObject = -> PsuTopAndBottom001 [Pad.Edge177]
  Diameter = 2
  Invert = true
  LeftHanded = false
  Length = 4
  LengthCustom = 50
  MatchOuter = false
  Offset = -50
  OffsetAngle = 0
  Placement = pos=(106.75,127.227,-110.492) rot=(1,0,0;1.5708rad)
  ScrewLength = 6
  Thread = false
  Type = 0
  Width = 0
FEATURE [Assembly::AssemblyObject] Assembly  label="PsuAssembly"
  Group = -> [Joints,PsuTopAndBottom,GroundedJoint,PsuTopAndBottom001,PsuSideShort,PsuSideShort001,PsuSideLong,PsuSideLong001,PowerEntry,Joint,Joint001,Joint002,Joint003,Joint004,Joint007,Psu,Joint008,Standoff,Standoff001,Standoff002,Standoff003,Standoff004,Standoff005,Standoff006,Standoff007]
  Origin = -> Origin
  Type = Assembly
---- part row.FCStd = doc fcstd_40c34ed43f45 ----
FCSTD DOCUMENT  (FreeCAD 1.0R38641 +468 (Git))
Label: row
License: All rights reserved
LicenseURL: https://en.wikipedia.org/wiki/All_rights_reserved
objects: App::FeaturePython×17, App::Link×14, Assembly::JointGroup×1, Assembly::AssemblyObject×1
EXTERNAL_REF file=third_party/tiptop_z_rail.FCStd obj=Body
EXTERNAL_REF file=parts/panel_side.FCStd obj=Body001
EXTERNAL_REF file=parts/panel_top_and_bottom.FCStd obj=Body
EXTERNAL_REF file=parts/panel_back.FCStd obj=Body
EXTERNAL_REF file=parts/dimensions.FCStd obj=VarSet
EXTERNAL_REF file=parts/frame_panel_spacer.FCStd obj=Body
EXTERNAL_REF file=parts/frame_bracket.FCStd obj=Body
EXTERNAL_REF file=third_party/doepfer_bus_board_v6.FCStd obj=Body

FEATURE [App::Link] ZRail84Hp
  LinkedObject = -> <external third_party/tiptop_z_rail.FCStd>#Body
FEATURE [App::FeaturePython] GroundedJoint  # Assembly grounded joint (typed FeaturePython)
  ObjectToGround = -> ZRail84Hp
FEATURE [App::Link] ZRail84Hp001
  LinkPlacement = pos=(427,3.84e-14,-112.5) rot=(0,1,0;3.14159rad)
  LinkedObject = -> <external third_party/tiptop_z_rail.FCStd>#Body
  Placement = pos=(427,3.84e-14,-112.5) rot=(0,1,0;3.14159rad)
FEATURE [App::Link] PanelSide
  LinkPlacement = pos=(2.1e-15,-4.56e-14,-3e-16) rot=(0,0,1;0rad)
  LinkedObject = -> <external parts/panel_side.FCStd>#Body001
  Placement = pos=(2.1e-15,-4.56e-14,-3e-16) rot=(0,0,1;0rad)
FEATURE [App::Link] PanelSide001
  LinkPlacement = pos=(428.854,-6e-16,4e-16) rot=(0,0,1;0rad)
  LinkedObject = -> <external parts/panel_side.FCStd>#Body001
  Placement = pos=(428.854,-6e-16,4e-16) rot=(0,0,1;0rad)
FEATURE [App::Link] PanelTopAndBottom
  LinkPlacement = pos=(5.0165e-12,3e-16,-2.004e-13) rot=(0,0,1;0rad)
  LinkedObject = -> <external parts/panel_top_and_bottom.FCStd>#Body
  Placement = pos=(5.0165e-12,3e-16,-2.004e-13) rot=(0,0,1;0rad)
FEATURE [App::Link] PanelTopAndBottom001
  LinkPlacement = pos=(5.0396e-12,-3.3e-14,-122.5) rot=(0,0,1;0rad)
  LinkedObject = -> <external parts/panel_top_and_bottom.FCStd>#Body
  Placement = pos=(5.0396e-12,-3.3e-14,-122.5) rot=(0,0,1;0rad)
FEATURE [App::Link] PanelBack
  LinkPlacement = pos=(5.0317e-12,1.81e-14,-2.019e-13) rot=(0,0,1;0rad)
  LinkedObject = -> <external parts/panel_back.FCStd>#Body
  Placement = pos=(5.0317e-12,1.81e-14,-2.019e-13) rot=(0,0,1;0rad)
FEATURE [App::FeaturePython] Joint  label="Fixed"  # Assembly joint (typed FeaturePython)
  Activated = true
  AngleMax = 0
  AngleMin = 0
  Detach1 = false
  Detach2 = false
  Distance = 0
  Distance2 = 0
  EnableAngleMax = false
  EnableAngleMin = false
  EnableLengthMax = false
  EnableLengthMin = false
  JointType = 0 (Fixed)
  LengthMax = 0
  LengthMin = 0
  Placement1 = pos=(1e-15,14.3,-117.5) rot=(0.57735,0.57735,0.57735;2.0944rad)
  Placement2 = pos=(0,14.3,5) rot=(0.57735,0.57735,0.57735;2.0944rad)
  Reference1 = -> Assembly [PanelSide.Edge71,PanelSide.Edge71]
  Reference2 = -> Assembly [ZRail84Hp.Edge33,ZRail84Hp.Edge33]
FEATURE [App::FeaturePython] Joint001  label="Fixed001"  # Assembly joint (typed FeaturePython)
  Activated = true
  AngleMax = 0
  AngleMin = 0
  Detach1 = false
  Detach2 = false
  Distance = 0
  Distance2 = 0
  EnableAngleMax = false
  EnableAngleMin = false
  EnableLengthMax = false
  EnableLengthMin = false
  JointType = 0 (Fixed)
  LengthMax = 0
  LengthMin = 0
  Placement1 = pos=(1e-15,14.3,5) rot=(0.57735,0.57735,0.57735;2.0944rad)
  Placement2 = pos=(427,14.3,5) rot=(0.57735,0.57735,0.57735;2.0944rad)
  Reference1 = -> Assembly [PanelSide.Edge68,PanelSide.Edge68]
  Reference2 = -> Assembly [ZRail84Hp001.Edge34,ZRail84Hp001.Edge34]
FEATURE [App::FeaturePython] Joint002  label="Fixed002"  # Assembly joint (typed FeaturePython)
  Activated = true
  AngleMax = 0
  AngleMin = 0
  Detach1 = false
  Detach2 = false
  Distance = 0
  Distance2 = 0
  EnableAngleMax = false
  EnableAngleMin = false
  EnableLengthMax = false
  EnableLengthMin = false
  JointType = 0 (Fixed)
  LengthMax = 0
  LengthMin = 0
  Placement1 = pos=(-1.8542,14.3,-117.5) rot=(0.57735,0.57735,0.57735;2.0944rad)
  Placement2 = pos=(427,14.3,5) rot=(0.57735,0.57735,0.57735;2.0944rad)
  Reference1 = -> Assembly [PanelSide001.Edge72,PanelSide001.Edge72]
  Reference2 = -> Assembly [ZRail84Hp.Edge34,ZRail84Hp.Edge34]
FEATURE [App::FeaturePython] Joint003  label="Fixed003"  # Assembly joint (typed FeaturePython)
  Activated = true
  AngleMax = 0
  AngleMin = 0
  Detach1 = false
  Detach2 = false
  Distance = 0
  Distance2 = 0
  EnableAngleMax = false
  EnableAngleMin = false
  EnableLengthMax = false
  EnableLengthMin = false
  JointType = 0 (Fixed)
  LengthMax = 0
  LengthMin = 0
  Placement1 = pos=(0,14.3,5) rot=(0.57735,0.57735,0.57735;2.0944rad)
  Placement2 = pos=(-1.8542,14.3,5) rot=(0.57735,0.57735,0.57735;2.0944rad)
  Reference1 = -> Assembly [ZRail84Hp001.Edge33,ZRail84Hp001.Edge33]
  Reference2 = -> Assembly [PanelSide001.Edge69,PanelSide001.Edge69]
FEATURE [App::FeaturePython] Joint004  label="Fixed004"  # Assembly joint (typed FeaturePython)
  Activated = true
  AngleMax = 0
  AngleMin = 0
  Detach1 = false
  Detach2 = false
  Distance = 0
  Distance2 = 0
  EnableAngleMax = false
  EnableAngleMin = false
  EnableLengthMax = false
  EnableLengthMin = false
  JointType = 0 (Fixed)
  LengthMax = 0
  LengthMin = 0
  Offset1 = pos=(-0.127,0.254,0) rot=(0,0,1;0rad)
  Offset2 = pos=(0,0,0) rot=(0,0,1;3.14159rad)
  Placement1 = pos=(427.927,31.925,3.9459) rot=(0.707107,0,0.707107;3.14159rad)
  Placement2 = pos=(-0.9271,127.354,-23.125) rot=(0,1,0;4.71239rad)
  Reference1 = -> Assembly [PanelTopAndBottom.Edge39,PanelTopAndBottom.Edge39]
  Reference2 = -> Assembly [PanelSide001.Edge37,PanelSide001.Edge37]
  expr: .Offset1.Base.x = -dimensions#VarSet.EnclosureFinishThickness
  expr: .Offset1.Base.y = 2 * dimensions#VarSet.EnclosureFinishThickness
FEATURE [App::FeaturePython] Joint005  label="Fixed005"  # Assembly joint (typed FeaturePython)
  Activated = true
  AngleMax = 0
  AngleMin = 0
  Detach1 = false
  Detach2 = false
  Distance = 0
  Distance2 = 0
  EnableAngleMax = false
  EnableAngleMin = false
  EnableLengthMax = false
  EnableLengthMin = false
  JointType = 0 (Fixed)
  LengthMax = 0
  LengthMin = 0
  Offset1 = pos=(0.127,-0.254,0) rot=(0,0,1;0rad)
  Offset2 = pos=(0,0,0) rot=(0,0,1;3.14159rad)
  Placement1 = pos=(-0.9271,32.179,3.8189) rot=(-0.707107,0,0.707107;3.14159rad)
  Placement2 = pos=(427.927,32.179,5.9271) rot=(0,-1,0;4.71239rad)
  Reference1 = -> Assembly [PanelSide001.Edge49,PanelSide001.Edge49]
  Reference2 = -> Assembly [PanelTopAndBottom001.Edge40,PanelTopAndBottom001.Edge40]
  expr: .Offset1.Base.x = dimensions#VarSet.EnclosureFinishThickness
  expr: .Offset1.Base.y = -2 * dimensions#VarSet.EnclosureFinishThickness
FEATURE [App::FeaturePython] Joint006  label="Fixed006"  # Assembly joint (typed FeaturePython)
  Activated = true
  AngleMax = 0
  AngleMin = 0
  Detach1 = false
  Detach2 = false
  Distance = 0
  Distance2 = 0
  EnableAngleMax = false
  EnableAngleMin = false
  EnableLengthMax = false
  EnableLengthMin = false
  JointType = 0 (Fixed)
  LengthMax = 0
  LengthMin = 0
  Offset1 = pos=(-0.254,-0.127,0) rot=(0,0,1;0rad)
  Placement1 = pos=(139.621,127.227,5) rot=(0,0,1;0rad)
  Placement2 = pos=(139.621,127.227,5) rot=(0,0,1;0rad)
  Reference1 = -> Assembly [PanelTopAndBottom.Edge92,PanelTopAndBottom.Edge92]
  Reference2 = -> Assembly [PanelBack.Edge165,PanelBack.Edge165]
  expr: .Offset1.Base.x = -2 * dimensions#VarSet.EnclosureFinishThickness
  expr: .Offset1.Base.y = -dimensions#VarSet.EnclosureFinishThickness
FEATURE [App::Link] FramePanelSpacer
  LinkPlacement = pos=(2.1e-15,-3.6e-14,-3.1e-15) rot=(0,0,1;0rad)
  LinkedObject = -> <external parts/frame_panel_spacer.FCStd>#Body
  Placement = pos=(2.1e-15,-3.6e-14,-3.1e-15) rot=(0,0,1;0rad)
FEATURE [App::Link] FramePanelSpacer001
  LinkPlacement = pos=(433.883,-1.9e-15,2.7e-15) rot=(0,0,1;0rad)
  LinkedObject = -> <external parts/frame_panel_spacer.FCStd>#Body
  Placement = pos=(433.883,-1.9e-15,2.7e-15) rot=(0,0,1;0rad)
FEATURE [App::Link] FrameBracket
  LinkPlacement = pos=(-3.175,-3.44e-14,3.4e-15) rot=(0,0,1;0rad)
  LinkedObject = -> <external parts/frame_bracket.FCStd>#Body
  Placement = pos=(-3.175,-3.44e-14,3.4e-15) rot=(0,0,1;0rad)
FEATURE [App::Link] FrameBracket001
  LinkPlacement = pos=(-13.2334,-3.72e-14,-112.5) rot=(0,1,0;3.14159rad)
  LinkedObject = -> <external parts/frame_bracket.FCStd>#Body
  Placement = pos=(-13.2334,-3.72e-14,-112.5) rot=(0,1,0;3.14159rad)
FEATURE [App::Link] FrameBracket002
  LinkPlacement = pos=(433.35,7.3e-15,-112.5) rot=(0,1,0;3.14159rad)
  LinkedObject = -> <external parts/frame_bracket.FCStd>#Body
  Placement = pos=(433.35,7.3e-15,-112.5) rot=(0,1,0;3.14159rad)
FEATURE [App::Link] FrameBracket003
  LinkPlacement = pos=(437.058,3.9e-15,3.4e-15) rot=(0,0,1;0rad)
  LinkedObject = -> <external parts/frame_bracket.FCStd>#Body
  Placement = pos=(437.058,3.9e-15,3.4e-15) rot=(0,0,1;0rad)
FEATURE [App::FeaturePython] Joint007  label="Fixed007"  # Assembly joint (typed FeaturePython)
  Activated = true
  AngleMax = 0
  AngleMin = 0
  Detach1 = false
  Detach2 = false
  Distance = 0
  Distance2 = 0
  EnableAngleMax = false
  EnableAngleMin = false
  EnableLengthMax = false
  EnableLengthMin = false
  JointType = 0 (Fixed)
  LengthMax = 0
  LengthMin = 0
  Placement1 = pos=(-1.8542,56.923,-56.25) rot=(0.57735,0.57735,0.57735;2.0944rad)
  Placement2 = pos=(-1.8542,56.923,-56.25) rot=(0.57735,0.57735,0.57735;2.0944rad)
  Reference1 = -> Assembly [FramePanelSpacer.Edge44,FramePanelSpacer.Edge44]
  Reference2 = -> Assembly [PanelSide.Edge63,PanelSide.Edge63]
FEATURE [App::FeaturePython] Joint008  label="Fixed008"  # Assembly joint (typed FeaturePython)
  Activated = true
  AngleMax = 0
  AngleMin = 0
  Detach1 = false
  Detach2 = false
  Distance = 0
  Distance2 = 0
  EnableAngleMax = false
  EnableAngleMin = false
  EnableLengthMax = false
  EnableLengthMin = false
  JointType = 0 (Fixed)
  LengthMax = 0
  LengthMin = 0
  Placement1 = pos=(-1.8542,73.177,-56.25) rot=(0.57735,0.57735,0.57735;2.0944rad)
  Placement2 = pos=(-1.8542,73.177,-56.25) rot=(0.57735,0.57735,0.57735;2.0944rad)
  Reference1 = -> Assembly [PanelSide.Edge66,PanelSide.Edge66]
  Reference2 = -> Assembly [FramePanelSpacer.Edge41,FramePanelSpacer.Edge41]
FEATURE [App::FeaturePython] Joint009  label="Fixed009"  # Assembly joint (typed FeaturePython)
  Activated = true
  AngleMax = 0
  AngleMin = 0
  Detach1 = false
  Detach2 = false
  Distance = 0
  Distance2 = 0
  EnableAngleMax = false
  EnableAngleMin = false
  EnableLengthMax = false
  EnableLengthMin = false
  JointType = 0 (Fixed)
  LengthMax = 0
  LengthMin = 0
  Placement1 = pos=(0,73.177,-56.25) rot=(0.57735,0.57735,0.57735;2.0944rad)
  Placement2 = pos=(-5.0292,73.177,-56.25) rot=(0.57735,0.57735,0.57735;2.0944rad)
  Reference1 = -> Assembly [PanelSide001.Edge65,PanelSide001.Edge65]
  Reference2 = -> Assembly [FramePanelSpacer001.Edge42,FramePanelSpacer001.Edge42]
FEATURE [App::FeaturePython] Joint010  label="Fixed010"  # Assembly joint (typed FeaturePython)
  Activated = true
  AngleMax = 0
  AngleMin = 0
  Detach1 = false
  Detach2 = false
  Distance = 0
  Distance2 = 0
  EnableAngleMax = false
  EnableAngleMin = false
  EnableLengthMax = false
  EnableLengthMin = false
  JointType = 0 (Fixed)
  LengthMax = 0
  LengthMin = 0
  Placement1 = pos=(0,56.923,-56.25) rot=(0.57735,0.57735,0.57735;2.0944rad)
  Placement2 = pos=(-5.0292,56.923,-56.25) rot=(0.57735,0.57735,0.57735;2.0944rad)
  Reference1 = -> Assembly [PanelSide001.Edge62,PanelSide001.Edge62]
  Reference2 = -> Assembly [FramePanelSpacer001.Edge45,FramePanelSpacer001.Edge45]
FEATURE [App::FeaturePython] Joint011  label="Fixed011"  # Assembly joint (typed FeaturePython)
  Activated = true
  AngleMax = 0
  AngleMin = 0
  Detach1 = false
  Detach2 = false
  Distance = 0
  Distance2 = 0
  EnableAngleMax = false
  EnableAngleMin = false
  EnableLengthMax = false
  EnableLengthMin = false
  JointType = 0 (Fixed)
  LengthMax = 0
  LengthMin = 0
  Placement1 = pos=(-1.8542,56.923,-56.25) rot=(0.57735,0.57735,0.57735;2.0944rad)
  Placement2 = pos=(-5.0292,56.923,-56.25) rot=(0.57735,0.57735,0.57735;2.0944rad)
  Reference1 = -> Assembly [FramePanelSpacer001.Edge44,FramePanelSpacer001.Edge44]
  Reference2 = -> Assembly [FrameBracket003.Edge99,FrameBracket003.Edge99]
FEATURE [App::FeaturePython] Joint012  label="Fixed012"  # Assembly joint (typed FeaturePython)
  Activated = true
  AngleMax = 0
  AngleMin = 0
  Detach1 = false
  Detach2 = false
  Distance = 0
  Distance2 = 0
  EnableAngleMax = false
  EnableAngleMin = false
  EnableLengthMax = false
  EnableLengthMin = false
  JointType = 0 (Fixed)
  LengthMax = 0
  LengthMin = 0
  Placement1 = pos=(-1.8542,56.923,-56.25) rot=(0.57735,0.57735,0.57735;2.0944rad)
  Placement2 = pos=(-1.8542,56.923,-56.25) rot=(0.57735,0.57735,0.57735;2.0944rad)
  Reference1 = -> Assembly [FrameBracket002.Edge98,FrameBracket002.Edge98]
  Reference2 = -> Assembly [FrameBracket003.Edge98,FrameBracket003.Edge98]
FEATURE [App::FeaturePython] Joint013  label="Fixed013"  # Assembly joint (typed FeaturePython)
  Activated = true
  AngleMax = 0
  AngleMin = 0
  Detach1 = false
  Detach2 = false
  Distance = 0
  Distance2 = 0
  EnableAngleMax = false
  EnableAngleMin = false
  EnableLengthMax = false
  EnableLengthMin = false
  JointType = 0 (Fixed)
  LengthMax = 0
  LengthMin = 0
  Placement1 = pos=(-1.8542,56.923,-56.25) rot=(0.57735,0.57735,0.57735;2.0944rad)
  Placement2 = pos=(-5.0292,56.923,-56.25) rot=(0.57735,0.57735,0.57735;2.0944rad)
  Reference1 = -> Assembly [FrameBracket.Edge98,FrameBracket.Edge98]
  Reference2 = -> Assembly [FramePanelSpacer.Edge45,FramePanelSpacer.Edge45]
FEATURE [App::FeaturePython] Joint014  label="Fixed014"  # Assembly joint (typed FeaturePython)
  Activated = true
  AngleMax = 0
  AngleMin = 0
  Detach1 = false
  Detach2 = false
  Distance = 0
  Distance2 = 0
  EnableAngleMax = false
  EnableAngleMin = false
  EnableLengthMax = false
  EnableLengthMin = false
  JointType = 0 (Fixed)
  LengthMax = 0
  LengthMin = 0
  Placement1 = pos=(-5.0292,56.923,-56.25) rot=(0.57735,0.57735,0.57735;2.0944rad)
  Placement2 = pos=(-5.0292,56.923,-56.25) rot=(0.57735,0.57735,0.57735;2.0944rad)
  Reference1 = -> Assembly [FrameBracket001.Edge99,FrameBracket001.Edge99]
  Reference2 = -> Assembly [FrameBracket.Edge99,FrameBracket.Edge99]
FEATURE [App::Link] BusBoard
  LinkPlacement = pos=(17.92,121.373,-77.205) rot=(1,0,0;1.5708rad)
  LinkedObject = -> <external third_party/doepfer_bus_board_v6.FCStd>#Body
  Placement = pos=(17.92,121.373,-77.205) rot=(1,0,0;1.5708rad)
FEATURE [App::FeaturePython] Joint015  label="Fixed015"  # Assembly joint (typed FeaturePython)
  Activated = true
  AngleMax = 0
  AngleMin = 0
  Detach1 = false
  Detach2 = false
  Distance = 0
  Distance2 = 0
  EnableAngleMax = false
  EnableAngleMin = false
  EnableLengthMax = false
  EnableLengthMin = false
  JointType = 0 (Fixed)
  LengthMax = 0
  LengthMin = 0
  Offset2 = pos=(0,0,4) rot=(0,0,1;0rad)
  Placement1 = pos=(214.63,3.175,0) rot=(0,0,1;0rad)
  Placement2 = pos=(232.55,121.373,-74.03) rot=(1,0,0;1.5708rad)
  Reference1 = -> Assembly [BusBoard.Edge23,BusBoard.Edge23]
  Reference2 = -> Assembly [PanelBack.Edge237,PanelBack.Edge237]
FEATURE [Assembly::JointGroup] Joints
  Group = -> [GroundedJoint,Joint,Joint001,Joint002,Joint003,Joint004,Joint005,Joint006,Joint007,Joint008,Joint009,Joint010,Joint011,Joint012,Joint013,Joint014,Joint015]
FEATURE [Assembly::AssemblyObject] Assembly  label="Row"
  Group = -> [Joints,ZRail84Hp,GroundedJoint,ZRail84Hp001,PanelSide,PanelSide001,PanelTopAndBottom,PanelTopAndBottom001,PanelBack,Joint,Joint001,Joint002,Joint003,Joint004,Joint005,Joint006,FramePanelSpacer,FramePanelSpacer001,FrameBracket,FrameBracket001,FrameBracket002,FrameBracket003,Joint007,Joint008,Joint009,Joint010,Joint011,Joint012,Joint013,Joint014,BusBoard,Joint015]
  Origin = -> Origin
  Type = Assembly
